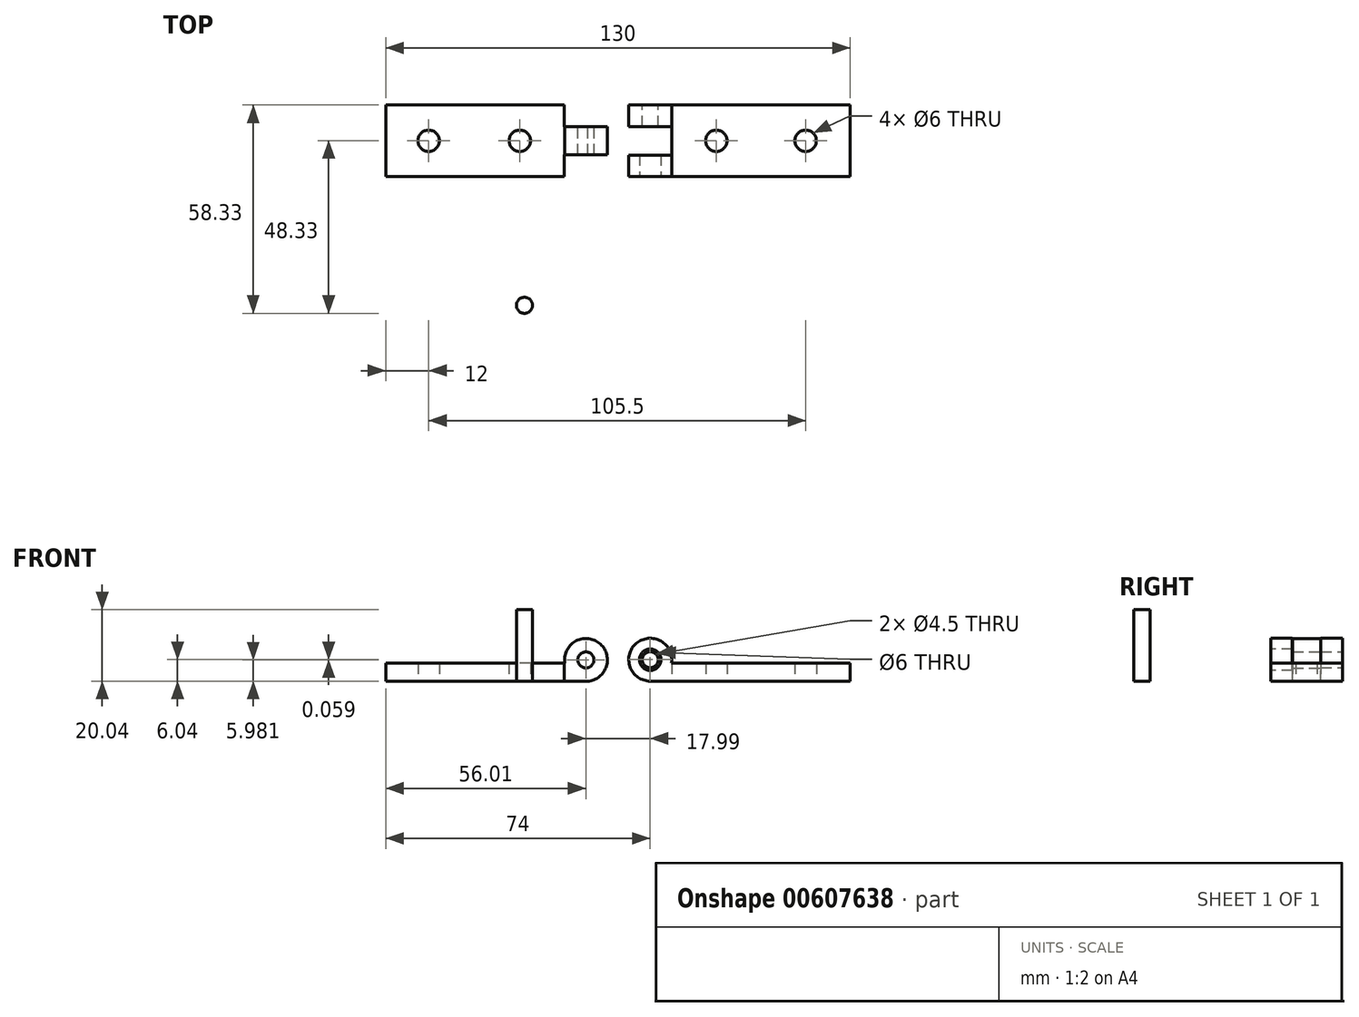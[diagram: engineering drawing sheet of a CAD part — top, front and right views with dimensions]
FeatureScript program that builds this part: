
annotation { "Feature Type Name" : "Feature", "Feature Type Description" : "" }
export const myFeature = defineFeature(function(context is Context, id is Id, definition is map)
    precondition{}
    {
        {
            var Q0;
            Q0=qCreatedBy(makeId("Top.planeOp"),FACE);
            var sketch = newSketch(context, id + "F0", { "sketchPlane" : qUnion([Q0])});
            skLineSegment(sketch, "E0.bottom", {"start": v(25, 10) * mm, "end": v(-25, 10) * mm});
            skLineSegment(sketch, "E0.top", {"start": v(25, -10) * mm, "end": v(-25, -10) * mm});
            skLineSegment(sketch, "E0.left", {"start": v(25, 10) * mm, "end": v(25, -10) * mm});
            skLineSegment(sketch, "E0.right", {"start": v(-25, 10) * mm, "end": v(-25, -10) * mm});
            skPoint(sketch, "E0.middle", {"position": v(0, 0) * mm});
            skCircle(sketch, "E1", {"center": v(-12.5, 0) * mm, "radius": 3 * mm});
            skCircle(sketch, "E2", {"center": v(12.5, 0) * mm, "radius": 3 * mm});
            skLineSegment(sketch, "E3.bottom", {"start": v(-55, -10) * mm, "end": v(-105, -10) * mm});
            skLineSegment(sketch, "E3.top", {"start": v(-55, 10) * mm, "end": v(-105, 10) * mm});
            skLineSegment(sketch, "E3.left", {"start": v(-55, -10) * mm, "end": v(-55, 10) * mm});
            skLineSegment(sketch, "E3.right", {"start": v(-105, -10) * mm, "end": v(-105, 10) * mm});
            skCircle(sketch, "E4", {"center": v(-67.5, 0) * mm, "radius": 3 * mm});
            skCircle(sketch, "E5", {"center": v(-93, 0) * mm, "radius": 3 * mm});
            skSolve(sketch);
        }
        {
            var Q0;
            Q0=makeQuery(id+"F0.imprint","IMPRINT",FACE,{"disambiguationData":[TD([[makeQuery(id+"F0.imprint","IMPRINT",EDGE,{"derivedFrom":sQuery(id+"F0.wireOp",EDGE,"E0.bottom")}),1.0]])]});
            var Q1;
            Q1=makeQuery(id+"F0.imprint","IMPRINT",FACE,{"disambiguationData":[TD([[makeQuery(id+"F0.imprint","IMPRINT",EDGE,{"derivedFrom":sQuery(id+"F0.wireOp",EDGE,"E3.bottom")}),-1.0]])]});
            extrude(context, id + "F1", {"entities" : qUnion([Q0, Q1]), "depth" : 5 * mm, "offsetDistance" : 25 * mm});
        }
        {
            var Q0;
            Q0=makeQuery(id+"F1.opExtrude","SWEPT_FACE",FACE,{"disambiguationData":[OSD([sQuery(id+"F0.wireOp",EDGE,"E0.top")])]});
            var sketch = newSketch(context, id + "F2", { "sketchPlane" : qUnion([Q0])});
            skArc(sketch, "E6", {"start": v(-25.08, 5) * mm, "mid": v(-34.87, 10.58) * mm, "end": v(-31, 0) * mm});
            skLineSegment(sketch, "E7", {"start": v(-25, 0) * mm, "end": v(-31, 0) * mm});
            skLineSegment(sketch, "E8.0", {"start": v(25, 5) * mm, "end": v(-25, 5) * mm});
            skLineSegment(sketch, "E8.1", {"start": v(25, 5) * mm, "end": v(25, 0) * mm});
            skLineSegment(sketch, "E8.2", {"start": v(25, 0) * mm, "end": v(-25, 0) * mm});
            skLineSegment(sketch, "E8.3", {"start": v(-25, 5) * mm, "end": v(-25, 0) * mm});
            skLineSegment(sketch, "E9", {"start": v(-25, 5) * mm, "end": v(-25.08, 5) * mm});
            skCircle(sketch, "E10", {"center": v(-31, 6) * mm, "radius": 3 * mm});
            skSolve(sketch);
        }
        {
            var Q0;
            Q0=makeQuery(id+"F2.imprint","IMPRINT",FACE,{"disambiguationData":[TD([[makeQuery(id+"F2.imprint","IMPRINT",EDGE,{"derivedFrom":sQuery(id+"F2.wireOp",EDGE,"E6")}),1.0]])]});
            extrude(context, id + "F3", {"entities" : qUnion([Q0]), "operationType" : NewBodyOperationType.ADD, "oppositeDirection" : true, "depth" : 6 * mm, "offsetDistance" : 25 * mm});
        }
        {
            var Q0;
            Q0=makeQuery(id+"F1.opExtrude","SWEPT_FACE",FACE,{"disambiguationData":[OSD([sQuery(id+"F0.wireOp",EDGE,"E0.bottom")])]});
            var sketch = newSketch(context, id + "F4", { "sketchPlane" : qUnion([Q0])});
            skLineSegment(sketch, "E11.0", {"start": v(-25, 5) * mm, "end": v(25, 5) * mm});
            skLineSegment(sketch, "E11.1", {"start": v(25, 5) * mm, "end": v(25, 0) * mm});
            skLineSegment(sketch, "E11.2", {"start": v(-25, 0) * mm, "end": v(25, 0) * mm});
            skLineSegment(sketch, "E11.3", {"start": v(25, 0) * mm, "end": v(31, 0) * mm});
            skArc(sketch, "E11.4", {"start": v(25.08, 5) * mm, "mid": v(34.87, 10.58) * mm, "end": v(31, 0) * mm});
            skLineSegment(sketch, "E11.5", {"start": v(25, 5) * mm, "end": v(25.08, 5) * mm});
            skCircle(sketch, "E12", {"center": v(31, 6) * mm, "radius": 3 * mm});
            skCircle(sketch, "E13", {"center": v(31, 6) * mm, "radius": 2.25 * mm});
            skSolve(sketch);
        }
        {
            var Q0;
            Q0=makeQuery(id+"F4.imprint","IMPRINT",FACE,{"disambiguationData":[TD([[makeQuery(id+"F4.imprint","IMPRINT",EDGE,{"derivedFrom":sQuery(id+"F4.wireOp",EDGE,"E11.1")}),1.0]])]});
            extrude(context, id + "F5", {"entities" : qUnion([Q0]), "operationType" : NewBodyOperationType.ADD, "oppositeDirection" : true, "depth" : 6 * mm, "offsetDistance" : 25 * mm});
        }
        {
            var Q0;
            Q0=makeQuery(id+"F1.opExtrude","SWEPT_FACE",FACE,{"disambiguationData":[OSD([sQuery(id+"F0.wireOp",EDGE,"E3.top")])]});
            var sketch = newSketch(context, id + "F6", { "sketchPlane" : qUnion([Q0])});
            skLineSegment(sketch, "E14.4", {"start": v(105, 5) * mm, "end": v(105, 0) * mm});
            skCircle(sketch, "E15", {"center": v(49, 5.94) * mm, "radius": 2.25 * mm});
            skLineSegment(sketch, "E16", {"start": v(48.51, -0.04) * mm, "end": v(55, 0) * mm});
            skLineSegment(sketch, "E17", {"start": v(55, 5) * mm, "end": v(54.92, 5) * mm});
            skPoint(sketch, "E14.0.start.orphan", {"position": v(25.08, 5) * mm});
            skArc(sketch, "E18", {"start": v(54.92, 5) * mm, "mid": v(45.28, 10.66) * mm, "end": v(48.51, -0.04) * mm});
            skLineSegment(sketch, "E19.0", {"start": v(55, 5) * mm, "end": v(55, 0) * mm});
            skSolve(sketch);
        }
        {
            var Q0;
            Q0=makeQuery(id+"F6.imprint","IMPRINT",FACE,{"disambiguationData":[TD([[makeQuery(id+"F6.imprint","IMPRINT",EDGE,{"derivedFrom":sQuery(id+"F6.wireOp",EDGE,"E15")}),-1.0]])]});
            extrude(context, id + "F7", {"entities" : qUnion([Q0]), "operationType" : NewBodyOperationType.ADD, "oppositeDirection" : true, "depth" : 13.9 * mm, "offsetDistance" : 25 * mm});
        }
        {
            var Q0;
            Q0=makeQuery(id+"F6.imprint","IMPRINT",FACE,{"disambiguationData":[TD([[makeQuery(id+"F6.imprint","IMPRINT",EDGE,{"derivedFrom":sQuery(id+"F6.wireOp",EDGE,"E15")}),-1.0]])]});
            extrude(context, id + "F8", {"entities" : qUnion([Q0]), "operationType" : NewBodyOperationType.REMOVE, "oppositeDirection" : true, "depth" : 6.1 * mm, "offsetDistance" : 25 * mm});
        }
        {
            var Q0;
            Q0=qCreatedBy(makeId("Top.planeOp"),FACE);
            var sketch = newSketch(context, id + "F9", { "sketchPlane" : qUnion([Q0])});
            skCircle(sketch, "E20", {"center": v(-66.19, -46.08) * mm, "radius": 2.25 * mm});
            skSolve(sketch);
        }
        {
            var Q0;
            Q0=makeQuery(id+"F9.imprint","IMPRINT",FACE,{"disambiguationData":[TD([[makeQuery(id+"F9.imprint","IMPRINT",EDGE,{"derivedFrom":sQuery(id+"F9.wireOp",EDGE,"E20")}),1.0]])]});
            extrude(context, id + "F10", {"entities" : qUnion([Q0]), "depth" : 20 * mm, "offsetDistance" : 25 * mm});
        }
        {
            var Q0;
            Q0=makeQuery(id+"F4.imprint","IMPRINT",FACE,{"disambiguationData":[TD([[makeQuery(id+"F4.imprint","IMPRINT",EDGE,{"derivedFrom":sQuery(id+"F4.wireOp",EDGE,"E12")}),1.0]])]});
            extrude(context, id + "F11", {"entities" : qUnion([Q0]), "operationType" : NewBodyOperationType.ADD, "oppositeDirection" : true, "depth" : 6 * mm, "offsetDistance" : 25 * mm});
        }
    });
